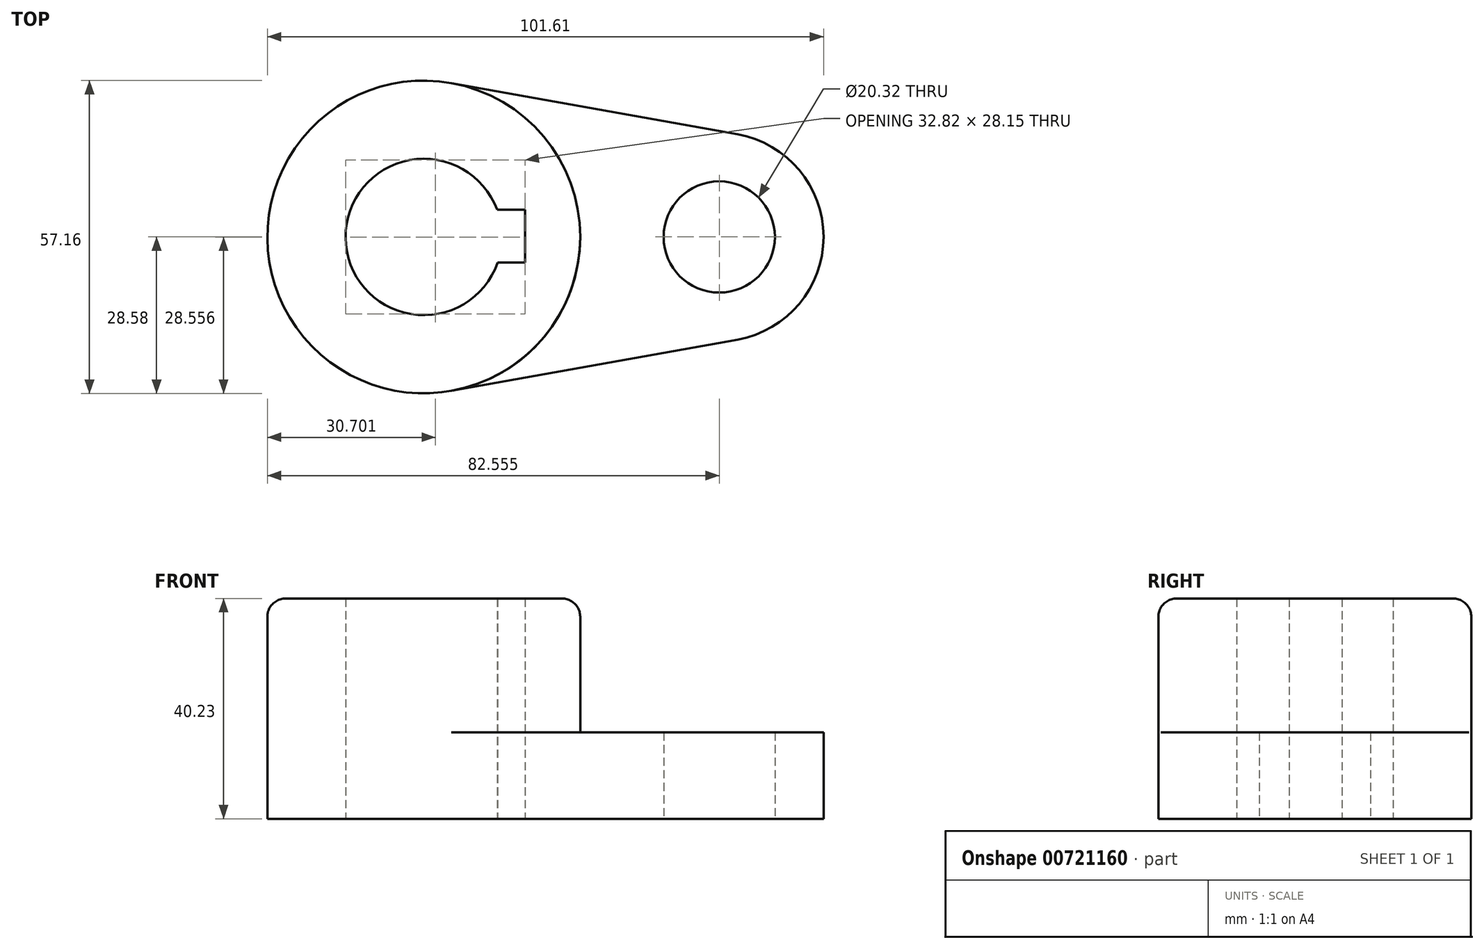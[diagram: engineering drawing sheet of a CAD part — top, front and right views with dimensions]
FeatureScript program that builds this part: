
annotation { "Feature Type Name" : "Feature", "Feature Type Description" : "" }
export const myFeature = defineFeature(function(context is Context, id is Id, definition is map)
    precondition{}
    {
        {
            var Q0;
            Q0=qCreatedBy(makeId("Top.planeOp"),FACE);
            var sketch = newSketch(context, id + "F0", { "sketchPlane" : qUnion([Q0])});
            skArc(sketch, "E0", {"start": v(13.4, 4.96) * mm, "mid": v(-14.29, -0.14) * mm, "end": v(13.5, -4.7) * mm});
            skCircle(sketch, "E1", {"center": v(0, 0) * mm, "radius": 28.58 * mm});
            skCircle(sketch, "E2", {"center": v(53.98, 0) * mm, "radius": 10.16 * mm});
            skLineSegment(sketch, "E3", {"start": v(13.4, 4.96) * mm, "end": v(18.53, 4.96) * mm});
            skLineSegment(sketch, "E4", {"start": v(18.53, 4.96) * mm, "end": v(18.53, -4.7) * mm});
            skLineSegment(sketch, "E5", {"start": v(18.53, -4.7) * mm, "end": v(13.5, -4.7) * mm});
            skArc(sketch, "E6", {"start": v(57.34, -18.75) * mm, "mid": v(73.03, 0) * mm, "end": v(57.34, 18.75) * mm});
            skLineSegment(sketch, "E7", {"start": v(5.04, 28.13) * mm, "end": v(57.34, 18.75) * mm});
            skLineSegment(sketch, "E8", {"start": v(5.04, -28.13) * mm, "end": v(57.34, -18.75) * mm});
            skSolve(sketch);
        }
        {
            var Q0;
            Q0=makeQuery(id+"F0.imprint","IMPRINT",FACE,{"disambiguationData":[TD([[makeQuery(id+"F0.imprint","IMPRINT",EDGE,{"derivedFrom":sQuery(id+"F0.wireOp",EDGE,"E2")}),-1.0]])]});
            extrude(context, id + "F1", {"entities" : qUnion([Q0]), "depth" : 15.77 * mm, "offsetDistance" : 25.4 * mm});
        }
        {
            var Q0;
            Q0=makeQuery(id+"F0.imprint","IMPRINT",FACE,{"disambiguationData":[TD([[makeQuery(id+"F0.imprint","IMPRINT",EDGE,{"derivedFrom":sQuery(id+"F0.wireOp",EDGE,"E0")}),-1.0]])]});
            extrude(context, id + "F2", {"entities" : qUnion([Q0]), "operationType" : NewBodyOperationType.ADD, "depth" : 40.23 * mm, "offsetDistance" : 25.4 * mm});
        }
        {
            var Q0;
            Q0=makeQuery(id+"F2.opExtrude","CAP_EDGE",EDGE,{"disambiguationData":[OSD([sQuery(id+"F0.wireOp",EDGE,"E1")])],"isStart":false});
            fillet(context, id + "F3", {"entities" : qUnion([Q0]), "radius" : 3.3 * mm, "tangentPropagation" : true, "allowEdgeOverflow" : false});
        }
    });
